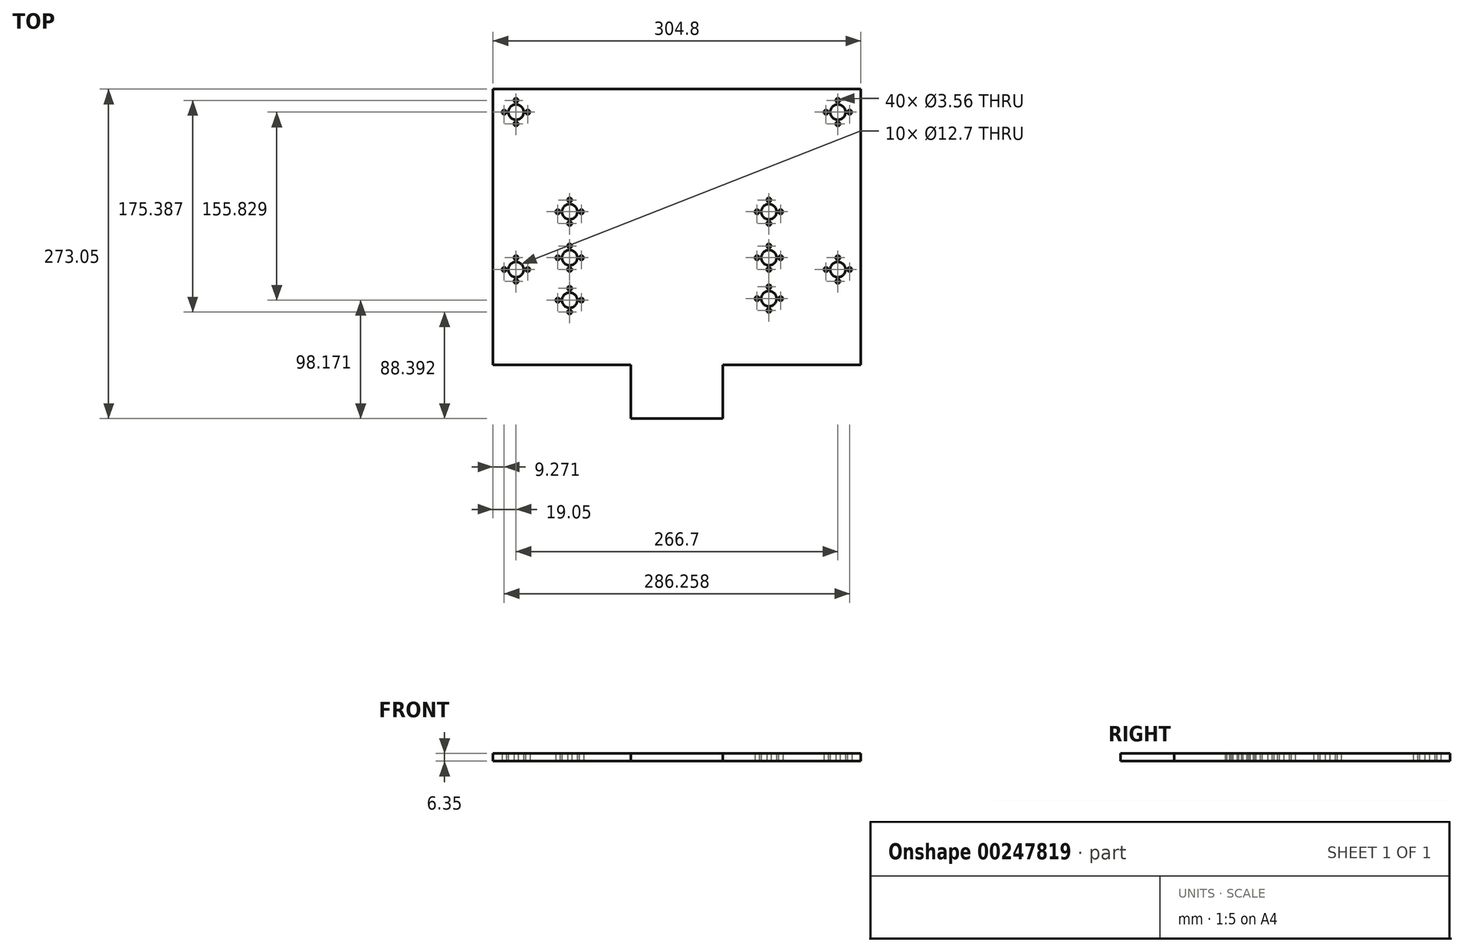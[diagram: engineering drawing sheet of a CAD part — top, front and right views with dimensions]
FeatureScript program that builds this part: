
annotation { "Feature Type Name" : "Feature", "Feature Type Description" : "" }
export const myFeature = defineFeature(function(context is Context, id is Id, definition is map)
    precondition{}
    {
        {
            var Q0;
            Q0=qCreatedBy(makeId("Top.planeOp"),FACE);
            var sketch = newSketch(context, id + "F0", { "sketchPlane" : qUnion([Q0])});
            skLineSegment(sketch, "E0.bottom", {"start": v(-152.4, 114.3) * mm, "end": v(152.4, 114.3) * mm});
            skLineSegment(sketch, "E0.top", {"start": v(-152.4, -114.3) * mm, "end": v(-38.1, -114.3) * mm});
            skLineSegment(sketch, "E0.left", {"start": v(-152.4, 114.3) * mm, "end": v(-152.4, -114.3) * mm});
            skLineSegment(sketch, "E0.right", {"start": v(152.4, 114.3) * mm, "end": v(152.4, -114.3) * mm});
            skPoint(sketch, "E0.middle", {"position": v(0, 0) * mm});
            skCircle(sketch, "E1", {"center": v(-133.35, 95.25) * mm, "radius": 6.35 * mm});
            skCircle(sketch, "E2", {"center": v(-133.35, 105.03) * mm, "radius": 1.78 * mm});
            skCircle(sketch, "E3.1.0", {"center": v(-143.13, 95.25) * mm, "radius": 1.78 * mm});
            skCircle(sketch, "E3.2.0", {"center": v(-133.35, 85.47) * mm, "radius": 1.78 * mm});
            skCircle(sketch, "E3.3.0", {"center": v(-123.57, 95.25) * mm, "radius": 1.78 * mm});
            skCircle(sketch, "E4.MirrorC", {"center": v(-133.35, -25.4) * mm, "radius": 1.78 * mm});
            skCircle(sketch, "E5", {"center": v(-133.35, -35.18) * mm, "radius": 6.35 * mm});
            skCircle(sketch, "E6.1.0", {"center": v(-143.13, -35.18) * mm, "radius": 1.78 * mm});
            skCircle(sketch, "E6.2.0", {"center": v(-133.35, -44.96) * mm, "radius": 1.78 * mm});
            skCircle(sketch, "E6.3.0", {"center": v(-123.57, -35.18) * mm, "radius": 1.78 * mm});
            skLineSegment(sketch, "E7.top", {"start": v(-38.1, -158.75) * mm, "end": v(38.1, -158.75) * mm});
            skLineSegment(sketch, "E7.left", {"start": v(-38.1, -114.3) * mm, "end": v(-38.1, -158.75) * mm});
            skLineSegment(sketch, "E7.right", {"start": v(38.1, -114.3) * mm, "end": v(38.1, -158.75) * mm});
            skPoint(sketch, "E8", {"position": v(0, -158.75) * mm});
            skCircle(sketch, "E9.MirrorC", {"center": v(133.35, -35.18) * mm, "radius": 6.35 * mm});
            skCircle(sketch, "E10.MirrorC", {"center": v(133.35, -44.96) * mm, "radius": 1.78 * mm});
            skCircle(sketch, "E11.MirrorC", {"center": v(123.57, -35.18) * mm, "radius": 1.78 * mm});
            skCircle(sketch, "E12.MirrorC", {"center": v(143.13, -35.18) * mm, "radius": 1.78 * mm});
            skCircle(sketch, "E13.MirrorC", {"center": v(133.35, -25.4) * mm, "radius": 1.78 * mm});
            skCircle(sketch, "E14.MirrorC", {"center": v(133.35, 85.47) * mm, "radius": 1.78 * mm});
            skCircle(sketch, "E15.MirrorC", {"center": v(123.57, 95.25) * mm, "radius": 1.78 * mm});
            skCircle(sketch, "E16.MirrorC", {"center": v(133.35, 105.03) * mm, "radius": 1.78 * mm});
            skCircle(sketch, "E17.MirrorC", {"center": v(143.13, 95.25) * mm, "radius": 1.78 * mm});
            skCircle(sketch, "E18.MirrorC", {"center": v(133.35, 95.25) * mm, "radius": 6.35 * mm});
            skLineSegment(sketch, "E19.trimOffspring", {"start": v(38.1, -114.3) * mm, "end": v(152.4, -114.3) * mm});
            skCircle(sketch, "E20.MirrorC", {"center": v(-88.9, -50.8) * mm, "radius": 1.78 * mm});
            skLineSegment(sketch, "E21", {"start": v(-88.9, -50.8) * mm, "end": v(-88.9, -60.58) * mm});
            skCircle(sketch, "E22", {"center": v(-88.9, -60.58) * mm, "radius": 6.35 * mm});
            skCircle(sketch, "E23.MirrorC", {"center": v(76.2, -49.53) * mm, "radius": 1.78 * mm});
            skCircle(sketch, "E24", {"center": v(76.2, -59.3) * mm, "radius": 6.35 * mm});
            skCircle(sketch, "E25.1.0", {"center": v(66.42, -59.3) * mm, "radius": 1.78 * mm});
            skCircle(sketch, "E25.2.0", {"center": v(76.2, -69.09) * mm, "radius": 1.78 * mm});
            skCircle(sketch, "E25.3.0", {"center": v(85.98, -59.3) * mm, "radius": 1.78 * mm});
            skCircle(sketch, "E26.MirrorC", {"center": v(76.2, 12.7) * mm, "radius": 6.35 * mm});
            skCircle(sketch, "E27.MirrorC", {"center": v(-88.9, 12.7) * mm, "radius": 6.35 * mm});
            skCircle(sketch, "E28.1.0", {"center": v(-98.68, -60.58) * mm, "radius": 1.78 * mm});
            skCircle(sketch, "E28.2.0", {"center": v(-88.9, -70.36) * mm, "radius": 1.78 * mm});
            skCircle(sketch, "E28.3.0", {"center": v(-79.12, -60.58) * mm, "radius": 1.78 * mm});
            skCircle(sketch, "E29.1.0", {"center": v(76.2, 22.48) * mm, "radius": 1.78 * mm});
            skCircle(sketch, "E30.1.0", {"center": v(66.42, 12.7) * mm, "radius": 1.78 * mm});
            skCircle(sketch, "E30.2.0", {"center": v(76.2, 2.92) * mm, "radius": 1.78 * mm});
            skCircle(sketch, "E30.3.0", {"center": v(85.98, 12.7) * mm, "radius": 1.78 * mm});
            skCircle(sketch, "E31.1.0", {"center": v(-88.9, 22.48) * mm, "radius": 1.78 * mm});
            skCircle(sketch, "E32.1.0", {"center": v(-98.68, 12.7) * mm, "radius": 1.78 * mm});
            skCircle(sketch, "E32.2.0", {"center": v(-88.9, 2.92) * mm, "radius": 1.78 * mm});
            skCircle(sketch, "E32.3.0", {"center": v(-79.12, 12.7) * mm, "radius": 1.78 * mm});
            skCircle(sketch, "E33.MirrorC", {"center": v(-88.9, -25.4) * mm, "radius": 6.35 * mm});
            skCircle(sketch, "E34.MirrorC", {"center": v(-88.9, -15.62) * mm, "radius": 1.78 * mm});
            skCircle(sketch, "E35.MirrorC", {"center": v(76.2, -15.62) * mm, "radius": 1.78 * mm});
            skCircle(sketch, "E36.MirrorC", {"center": v(76.2, -25.4) * mm, "radius": 6.35 * mm});
            skCircle(sketch, "E37.1.0", {"center": v(66.42, -25.4) * mm, "radius": 1.78 * mm});
            skCircle(sketch, "E37.2.0", {"center": v(76.2, -35.18) * mm, "radius": 1.78 * mm});
            skCircle(sketch, "E37.3.0", {"center": v(85.98, -25.4) * mm, "radius": 1.78 * mm});
            skCircle(sketch, "E38.1.0", {"center": v(-98.68, -25.4) * mm, "radius": 1.78 * mm});
            skCircle(sketch, "E38.2.0", {"center": v(-88.9, -35.18) * mm, "radius": 1.78 * mm});
            skCircle(sketch, "E38.3.0", {"center": v(-79.12, -25.4) * mm, "radius": 1.78 * mm});
            skSolve(sketch);
        }
        {
            var Q0;
            Q0=makeQuery(id+"F0.imprint","IMPRINT",FACE,{"disambiguationData":[TD([[makeQuery(id+"F0.imprint","IMPRINT",EDGE,{"derivedFrom":sQuery(id+"F0.wireOp",EDGE,"E0.bottom")}),-1.0]])]});
            extrude(context, id + "F1", {"entities" : qUnion([Q0]), "depth" : 6.35 * mm});
        }
    });
